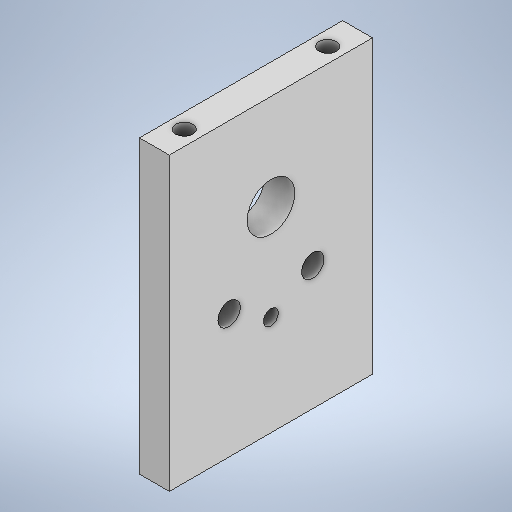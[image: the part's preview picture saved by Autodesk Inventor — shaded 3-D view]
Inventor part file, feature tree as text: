
AUTODESK INVENTOR PART (.ipt)
format: ipt  version: 2025.1 (Build 291241020, 241B)  size: 293,376 bytes
history: native  units: in
note: dims shown in document units (in); Inventor stores cm internally (conversion verified against a paired STEP export)
features: sketch x8, extrude x7, hole x1, projected_geometry x1
ambient origin geometry x8: Origin, YZ Plane, XZ Plane, XY Plane, X Axis, Y Axis, Z Axis, Center Point
bodies: Solid1 (feature_tree)
feature tree (17):
  extrude  "Extrusion1"  Depth=2.5in
  extrude  "Extrusion2"  Depth=0.0625in
  extrude  "Extrusion3"  Depth=0.0625in
  extrude  "Extrusion4"  Depth=0.3976in
  extrude  "Extrusion5"  TaperAngle=0.0deg  [1 undecoded]
  extrude  "Extrusion6"  Depth=0.8in
  extrude  "Extrusion7"  Depth=0.6in
  hole  "Hole1"  [1 undecoded]
  sketch  "Sketch1"  dims[d0=11.0in d1=2.5in]
  sketch  "Sketch2"  dims[d2=1.7in d3=0.0in d4=0.0625in]
  sketch  "Sketch3"  dims[d5=0.0625in d6=0.0625in]
  sketch  "Sketch4"  dims[d7=1.5in d8=0.0in d9=0.3976in]
  sketch  "Sketch5"  dims[d10=0.8in d11=0.0in d12=0.0in]
  sketch  "Sketch6"  dims[d13=0.125in d15=0.8in]
  sketch  "Sketch7"  dims[d16=0.5in d17=0.6in]
  projected_geometry  "Projected Loop1"
  sketch  "Sketch8"  dims[d18=0.1875in d19=1.0in d20=0.0in d21=0.125in d22=0.6102in d23=0.6102in d24=1.0in d25=0.0in d26=0.0in d27=0.0in d28=0.25in d29=0.0in d30=0.25in d31=0.25in d32=0.144in d33=0.75in d34=0.563in d35=0.12in d36=0.5635in d37=0.885in d38=0.8108in]
note: 2 required parameter values undecoded (feature->parameter linkage not recoverable at this tier; creation-order binding heuristic only, values carry confidence <= 0.55)
